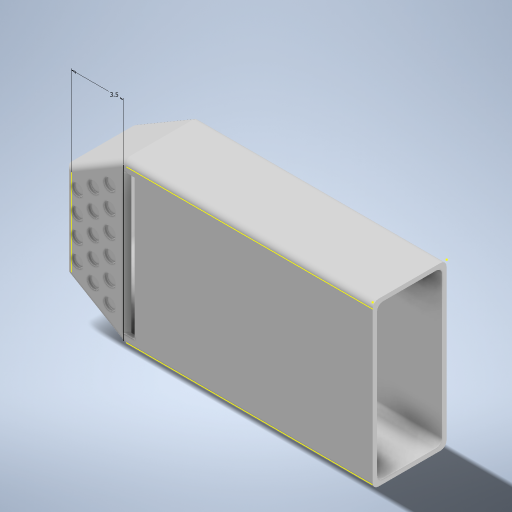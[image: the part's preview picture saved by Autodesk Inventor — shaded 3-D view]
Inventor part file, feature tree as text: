
AUTODESK INVENTOR PART (.ipt)
format: ipt  version: 2023.3 (Build 273359000, 359)  size: 421,888 bytes
history: native  units: mm
features: sketch x10, extrude x8, plane x2, fillet x1, projected_geometry x1
ambient origin geometry x8: Origin, YZ Plane, XZ Plane, XY Plane, X Axis, Y Axis, Z Axis, Center Point
bodies: Solid1 (feature_tree)
feature tree (22):
  extrude  "Extrusion1"  Depth=10.4mm
  extrude  "Extrusion2"  Depth=0.4mm
  extrude  "Extrusion3"  Depth=0.4mm
  extrude  "Extrusion4"  Depth=12.0mm
  fillet  "Fillet1"  Radius=0.5mm
  sketch  "Sketch5"  dims[d14=0.5mm d15=0.0mm d16=0.3mm]
  plane  "Work Plane1"
  sketch  "Sketch6"  dims[d17=0.3mm d18=5.0mm d19=0.0mm]
  plane  "Work Plane2"
  extrude  "Extrusion5"  Depth=0.3mm
  extrude  "Extrusion6"  Depth=5.0mm TaperAngle=0.0deg
  extrude  "Extrusion7"  Depth=20.777mm
  extrude  "Extrusion8"  Depth=3.5mm
  sketch  "Sketch1"  dims[d0=0.3mm d2=10.4mm]
  sketch  "Sketch2"  dims[d3=0.4mm d4=4.0mm]
  sketch  "Sketch3"  dims[d7=5.0mm d8=0.0mm d9=0.4mm]
  projected_geometry  "Projected Loop1"
  sketch  "Sketch4"  dims[d10=1.4mm d11=12.0mm d12=0.5mm d13=0.0mm]
  sketch  "Sketch7"  dims[d20=0.4mm d21=20.777mm]
  sketch  "Sketch8"  dims[d22=6.3mm d23=3.5mm]
  sketch  "Sketch9"  dims[d24=6.981317mm]
  sketch  "Sketch10"  dims[d25=-6.981317mm d26=9.5mm d27=0.6mm d28=3.0mm d29=0.0mm d30=9.5mm d31=0.6mm d32=3.0mm d33=0.0mm d34=0.8mm d35=0.8mm d36=1.4mm d37=1.4mm d38=1.4mm d39=0.8mm d40=1.4mm d41=1.4mm d42=1.4mm d43=1.4mm d44=1.4mm d45=6.3mm d46=3.15mm d47=1.4mm d48=1.4mm d49=1.4mm d51=1.4mm d52=1.1mm d53=1.1mm d54=0.2mm d55=0.0mm d56=0.2mm d57=0.0mm]
